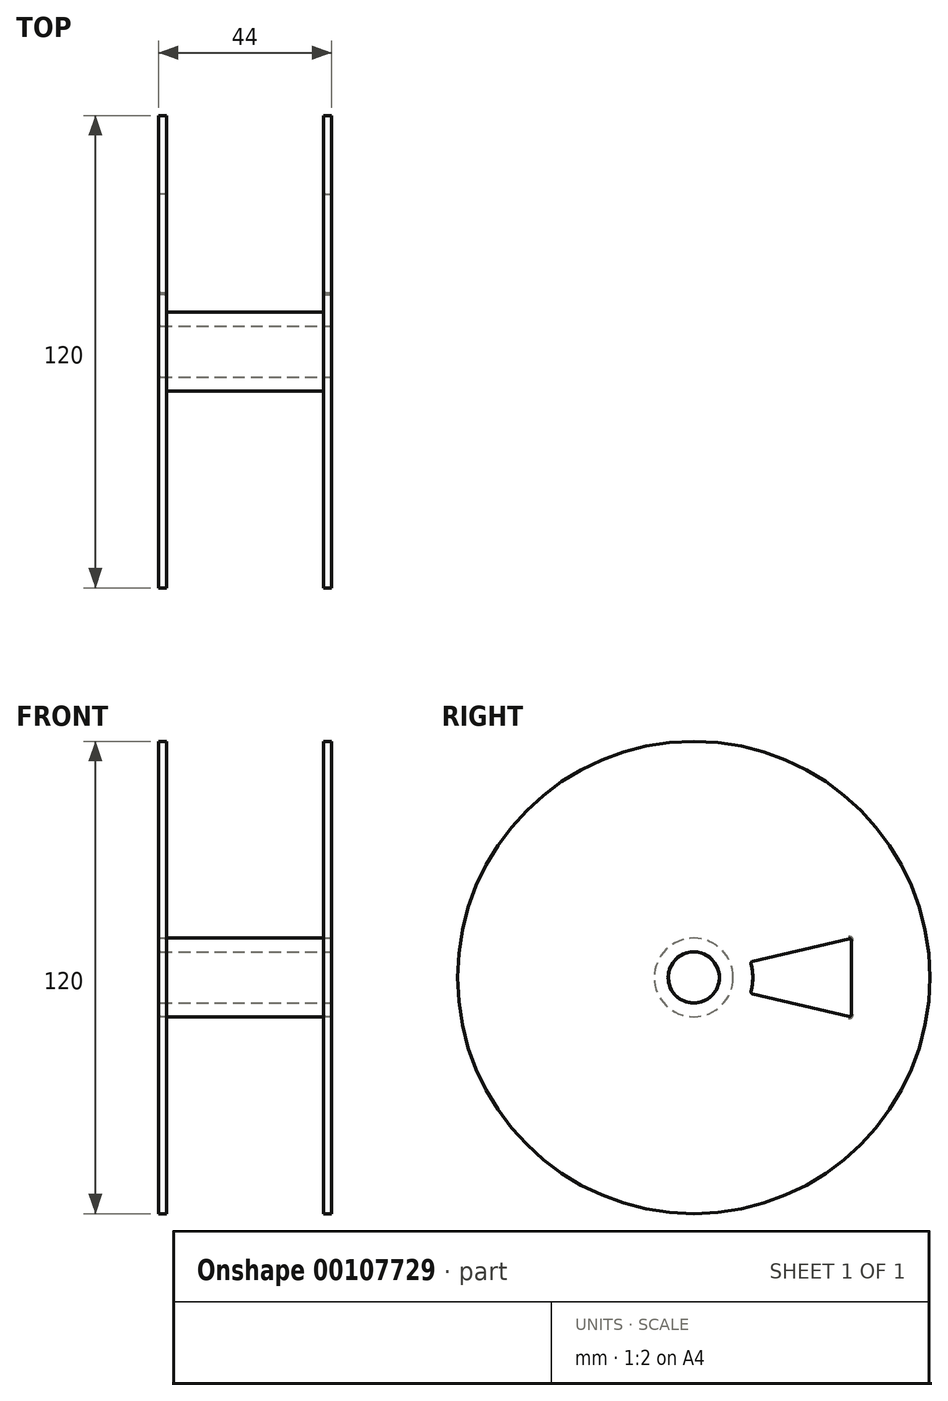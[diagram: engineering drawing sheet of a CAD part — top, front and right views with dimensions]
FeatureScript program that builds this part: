
annotation { "Feature Type Name" : "Feature", "Feature Type Description" : "" }
export const myFeature = defineFeature(function(context is Context, id is Id, definition is map)
    precondition{}
    {
        {
            var Q0;
            Q0=qCreatedBy(makeId("Front.planeOp"),FACE);
            var sketch = newSketch(context, id + "F0", { "sketchPlane" : qUnion([Q0])});
            skLineSegment(sketch, "E0", {"start": v(0, 0) * mm, "end": v(0, 10) * mm});
            skLineSegment(sketch, "E1", {"start": v(0, 10) * mm, "end": v(-20, 10) * mm});
            skLineSegment(sketch, "E2", {"start": v(-20, 10) * mm, "end": v(-20, 60) * mm});
            skLineSegment(sketch, "E3", {"start": v(-20, 60) * mm, "end": v(-22, 60) * mm});
            skLineSegment(sketch, "E4", {"start": v(-22, 60) * mm, "end": v(-22, 0) * mm});
            skLineSegment(sketch, "E5", {"start": v(-22, 0) * mm, "end": v(0, 0) * mm});
            skLineSegment(sketch, "E6.MirrorCS", {"start": v(20, 60) * mm, "end": v(22, 60) * mm});
            skLineSegment(sketch, "E7.MirrorCS", {"start": v(22, 0) * mm, "end": v(0, 0) * mm});
            skLineSegment(sketch, "E8.MirrorCS", {"start": v(20, 10) * mm, "end": v(20, 60) * mm});
            skLineSegment(sketch, "E9.MirrorCS", {"start": v(22, 60) * mm, "end": v(22, 0) * mm});
            skLineSegment(sketch, "E10.MirrorCS", {"start": v(0, 10) * mm, "end": v(20, 10) * mm});
            skSolve(sketch);
        }
        {
            var Q0;
            Q0 = qSketchRegion(id + "F0", true);
            var Q1;
            Q1=sQuery(id+"F0.wireOp",EDGE,"E5");
            revolve(context, id + "F1", {"entities" : qUnion([Q0]), "axis" : qUnion([Q1]), "revolveType" : RevolveType.FULL});
        }
        {
            var Q0;
            Q0=makeQuery(id+"F1.opRevolve","SWEPT_FACE",FACE,{"disambiguationData":[OSD([sQuery(id+"F0.wireOp",EDGE,"E9.MirrorCS")])]});
            var sketch = newSketch(context, id + "F2", { "sketchPlane" : qUnion([Q0])});
            skCircle(sketch, "E11", {"center": v(0, 0) * mm, "radius": 6.5 * mm});
            skSolve(sketch);
        }
        {
            var Q0;
            Q0 = qSketchRegion(id + "F2", true);
            extrude(context, id + "F3", {"entities" : qUnion([Q0]), "operationType" : NewBodyOperationType.REMOVE, "endBound" : BoundingType.THROUGH_ALL, "oppositeDirection" : true, "depth" : 25 * mm});
        }
        {
            var Q0;
            Q0=makeQuery(id+"F1.opRevolve","SWEPT_FACE",FACE,{"disambiguationData":[OSD([sQuery(id+"F0.wireOp",EDGE,"E9.MirrorCS")])]});
            var sketch = newSketch(context, id + "F4", { "sketchPlane" : qUnion([Q0])});
            skLineSegment(sketch, "E12", {"start": v(0, 0) * mm, "end": v(40, 0) * mm, "construction": true});
            skLineSegment(sketch, "E13", {"start": v(40, 10) * mm, "end": v(40, -10) * mm});
            skCircle(sketch, "E14.0", {"center": v(0, 0) * mm, "radius": 15 * mm});
            skLineSegment(sketch, "E15", {"start": v(40, 10) * mm, "end": v(14.46, 4) * mm});
            skLineSegment(sketch, "E16.MirrorCS", {"start": v(40, -10) * mm, "end": v(14.46, -4) * mm});
            skSolve(sketch);
        }
        {
            var Q0;
            Q0=makeQuery(id+"F4.imprint","IMPRINT",FACE,{"disambiguationData":[TD([[makeQuery(id+"F4.imprint","IMPRINT",EDGE,{"derivedFrom":sQuery(id+"F4.wireOp",EDGE,"E13")}),-1.0]])]});
            extrude(context, id + "F5", {"entities" : qUnion([Q0]), "operationType" : NewBodyOperationType.REMOVE, "endBound" : BoundingType.THROUGH_ALL, "oppositeDirection" : true, "depth" : 25 * mm});
        }
        {
            var Q0;
            Q0=makeQuery(id+"F5.boolean.opBoolean","COPY",EDGE,{"derivedFrom":makeQuery(id+"F5.opExtrude","CAP_EDGE",EDGE,{"disambiguationData":[OSD([sQuery(id+"F4.wireOp",EDGE,"E16.MirrorCS")])],"isStart":true})});
            var Q1;
            Q1=makeQuery(id+"F5.boolean.opBoolean","INTERSECT",EDGE,{"derivedFrom":[makeQuery(id+"F1.opRevolve","SWEPT_FACE",FACE,{"disambiguationData":[OSD([sQuery(id+"F0.wireOp",EDGE,"E8.MirrorCS")])]}),makeQuery(id+"F5.opExtrude","SWEPT_FACE",FACE,{"disambiguationData":[OSD([sQuery(id+"F4.wireOp",EDGE,"E13")])]})]});
            var Q2;
            Q2=makeQuery(id+"F5.boolean.opBoolean","COPY",EDGE,{"derivedFrom":makeQuery(id+"F5.opExtrude","CAP_EDGE",EDGE,{"disambiguationData":[OSD([sQuery(id+"F4.wireOp",EDGE,"E15")])],"isStart":true})});
            var Q3;
            Q3=makeQuery(id+"F5.boolean.opBoolean","INTERSECT",EDGE,{"derivedFrom":[makeQuery(id+"F1.opRevolve","SWEPT_FACE",FACE,{"disambiguationData":[OSD([sQuery(id+"F0.wireOp",EDGE,"E8.MirrorCS")])]}),makeQuery(id+"F5.opExtrude","SWEPT_FACE",FACE,{"disambiguationData":[OSD([sQuery(id+"F4.wireOp",EDGE,"E16.MirrorCS")])]})]});
            var Q4;
            Q4=makeQuery(id+"F5.boolean.opBoolean","INTERSECT",EDGE,{"derivedFrom":[makeQuery(id+"F1.opRevolve","SWEPT_FACE",FACE,{"disambiguationData":[OSD([sQuery(id+"F0.wireOp",EDGE,"E8.MirrorCS")])]}),makeQuery(id+"F5.opExtrude","SWEPT_FACE",FACE,{"disambiguationData":[OSD([sQuery(id+"F4.wireOp",EDGE,"E15")])]})]});
            var Q5;
            Q5=makeQuery(id+"F5.boolean.opBoolean","COPY",EDGE,{"derivedFrom":makeQuery(id+"F5.opExtrude","CAP_EDGE",EDGE,{"disambiguationData":[OSD([sQuery(id+"F4.wireOp",EDGE,"E14.0")])],"isStart":true})});
            var Q6;
            Q6=makeQuery(id+"F5.boolean.opBoolean","COPY",EDGE,{"derivedFrom":makeQuery(id+"F5.opExtrude","CAP_EDGE",EDGE,{"disambiguationData":[OSD([sQuery(id+"F4.wireOp",EDGE,"E13")])],"isStart":true})});
            var Q7;
            Q7=makeQuery(id+"F5.boolean.opBoolean","COPY",EDGE,{"disambiguationData":[OD(0.0)],"derivedFrom":makeQuery(id+"F5.opExtrude","SWEPT_EDGE",EDGE,{"disambiguationData":[OSD([sQuery(id+"F4.wireOp",EDGE,"E14.0"),sQuery(id+"F4.wireOp",EDGE,"E16.MirrorCS")])]})});
            var Q8;
            Q8=makeQuery(id+"F5.boolean.opBoolean","COPY",EDGE,{"disambiguationData":[OD(0.0)],"derivedFrom":makeQuery(id+"F5.opExtrude","SWEPT_EDGE",EDGE,{"disambiguationData":[OSD([sQuery(id+"F4.wireOp",EDGE,"E14.0"),sQuery(id+"F4.wireOp",EDGE,"E15")])]})});
            var Q9;
            Q9=makeQuery(id+"F5.boolean.opBoolean","COPY",EDGE,{"disambiguationData":[OD(0.0)],"derivedFrom":makeQuery(id+"F5.opExtrude","SWEPT_EDGE",EDGE,{"disambiguationData":[OSD([sQuery(id+"F4.wireOp",EDGE,"E13"),sQuery(id+"F4.wireOp",EDGE,"E15")])]})});
            var Q10;
            Q10=makeQuery(id+"F5.boolean.opBoolean","INTERSECT",EDGE,{"derivedFrom":[makeQuery(id+"F1.opRevolve","SWEPT_FACE",FACE,{"disambiguationData":[OSD([sQuery(id+"F0.wireOp",EDGE,"E2")])]}),makeQuery(id+"F5.opExtrude","SWEPT_FACE",FACE,{"disambiguationData":[OSD([sQuery(id+"F4.wireOp",EDGE,"E16.MirrorCS")])]})]});
            var Q11;
            Q11=makeQuery(id+"F5.boolean.opBoolean","INTERSECT",EDGE,{"derivedFrom":[makeQuery(id+"F1.opRevolve","SWEPT_FACE",FACE,{"disambiguationData":[OSD([sQuery(id+"F0.wireOp",EDGE,"E8.MirrorCS")])]}),makeQuery(id+"F5.opExtrude","SWEPT_FACE",FACE,{"disambiguationData":[OSD([sQuery(id+"F4.wireOp",EDGE,"E14.0")])]})]});
            var Q12;
            Q12=makeQuery(id+"F5.boolean.opBoolean","INTERSECT",EDGE,{"derivedFrom":[makeQuery(id+"F1.opRevolve","SWEPT_FACE",FACE,{"disambiguationData":[OSD([sQuery(id+"F0.wireOp",EDGE,"E4")])]}),makeQuery(id+"F5.opExtrude","SWEPT_FACE",FACE,{"disambiguationData":[OSD([sQuery(id+"F4.wireOp",EDGE,"E16.MirrorCS")])]})]});
            var Q13;
            Q13=makeQuery(id+"F5.boolean.opBoolean","COPY",EDGE,{"disambiguationData":[OD(0.0)],"derivedFrom":makeQuery(id+"F5.opExtrude","SWEPT_EDGE",EDGE,{"disambiguationData":[OSD([sQuery(id+"F4.wireOp",EDGE,"E13"),sQuery(id+"F4.wireOp",EDGE,"E16.MirrorCS")])]})});
            var Q14;
            Q14=makeQuery(id+"F5.boolean.opBoolean","COPY",EDGE,{"disambiguationData":[OD(1.0)],"derivedFrom":makeQuery(id+"F5.opExtrude","SWEPT_EDGE",EDGE,{"disambiguationData":[OSD([sQuery(id+"F4.wireOp",EDGE,"E14.0"),sQuery(id+"F4.wireOp",EDGE,"E16.MirrorCS")])]})});
            var Q15;
            Q15=makeQuery(id+"F5.boolean.opBoolean","COPY",EDGE,{"disambiguationData":[OD(1.0)],"derivedFrom":makeQuery(id+"F5.opExtrude","SWEPT_EDGE",EDGE,{"disambiguationData":[OSD([sQuery(id+"F4.wireOp",EDGE,"E13"),sQuery(id+"F4.wireOp",EDGE,"E16.MirrorCS")])]})});
            var Q16;
            Q16=makeQuery(id+"F5.boolean.opBoolean","INTERSECT",EDGE,{"derivedFrom":[makeQuery(id+"F1.opRevolve","SWEPT_FACE",FACE,{"disambiguationData":[OSD([sQuery(id+"F0.wireOp",EDGE,"E2")])]}),makeQuery(id+"F5.opExtrude","SWEPT_FACE",FACE,{"disambiguationData":[OSD([sQuery(id+"F4.wireOp",EDGE,"E15")])]})]});
            var Q17;
            Q17=makeQuery(id+"F5.boolean.opBoolean","INTERSECT",EDGE,{"derivedFrom":[makeQuery(id+"F1.opRevolve","SWEPT_FACE",FACE,{"disambiguationData":[OSD([sQuery(id+"F0.wireOp",EDGE,"E2")])]}),makeQuery(id+"F5.opExtrude","SWEPT_FACE",FACE,{"disambiguationData":[OSD([sQuery(id+"F4.wireOp",EDGE,"E14.0")])]})]});
            var Q18;
            Q18=makeQuery(id+"F5.boolean.opBoolean","INTERSECT",EDGE,{"derivedFrom":[makeQuery(id+"F1.opRevolve","SWEPT_FACE",FACE,{"disambiguationData":[OSD([sQuery(id+"F0.wireOp",EDGE,"E4")])]}),makeQuery(id+"F5.opExtrude","SWEPT_FACE",FACE,{"disambiguationData":[OSD([sQuery(id+"F4.wireOp",EDGE,"E15")])]})]});
            var Q19;
            Q19=makeQuery(id+"F5.boolean.opBoolean","INTERSECT",EDGE,{"derivedFrom":[makeQuery(id+"F1.opRevolve","SWEPT_FACE",FACE,{"disambiguationData":[OSD([sQuery(id+"F0.wireOp",EDGE,"E4")])]}),makeQuery(id+"F5.opExtrude","SWEPT_FACE",FACE,{"disambiguationData":[OSD([sQuery(id+"F4.wireOp",EDGE,"E14.0")])]})]});
            var Q20;
            Q20=makeQuery(id+"F5.boolean.opBoolean","INTERSECT",EDGE,{"derivedFrom":[makeQuery(id+"F1.opRevolve","SWEPT_FACE",FACE,{"disambiguationData":[OSD([sQuery(id+"F0.wireOp",EDGE,"E4")])]}),makeQuery(id+"F5.opExtrude","SWEPT_FACE",FACE,{"disambiguationData":[OSD([sQuery(id+"F4.wireOp",EDGE,"E13")])]})]});
            var Q21;
            Q21=makeQuery(id+"F5.boolean.opBoolean","INTERSECT",EDGE,{"derivedFrom":[makeQuery(id+"F1.opRevolve","SWEPT_FACE",FACE,{"disambiguationData":[OSD([sQuery(id+"F0.wireOp",EDGE,"E2")])]}),makeQuery(id+"F5.opExtrude","SWEPT_FACE",FACE,{"disambiguationData":[OSD([sQuery(id+"F4.wireOp",EDGE,"E13")])]})]});
            var Q22;
            Q22=makeQuery(id+"F5.boolean.opBoolean","COPY",EDGE,{"disambiguationData":[OD(1.0)],"derivedFrom":makeQuery(id+"F5.opExtrude","SWEPT_EDGE",EDGE,{"disambiguationData":[OSD([sQuery(id+"F4.wireOp",EDGE,"E14.0"),sQuery(id+"F4.wireOp",EDGE,"E15")])]})});
            var Q23;
            Q23=makeQuery(id+"F5.boolean.opBoolean","COPY",EDGE,{"disambiguationData":[OD(1.0)],"derivedFrom":makeQuery(id+"F5.opExtrude","SWEPT_EDGE",EDGE,{"disambiguationData":[OSD([sQuery(id+"F4.wireOp",EDGE,"E13"),sQuery(id+"F4.wireOp",EDGE,"E15")])]})});
            var Q24;
            Q24=makeQuery(id+"F3.boolean.opBoolean","COPY",EDGE,{"derivedFrom":makeQuery(id+"F3.opExtrude","CAP_EDGE",EDGE,{"disambiguationData":[OSD([sQuery(id+"F2.wireOp",EDGE,"E11")])],"isStart":true})});
            var Q25;
            Q25=makeQuery(id+"F3.boolean.opBoolean","INTERSECT",EDGE,{"derivedFrom":[makeQuery(id+"F1.opRevolve","SWEPT_FACE",FACE,{"disambiguationData":[OSD([sQuery(id+"F0.wireOp",EDGE,"E4")])]}),makeQuery(id+"F3.opExtrude","SWEPT_FACE",FACE,{"disambiguationData":[OSD([sQuery(id+"F2.wireOp",EDGE,"E11")])]})]});
            fillet(context, id + "F6", {"entities" : qUnion([Q0, Q1, Q2, Q3, Q4, Q5, Q6, Q7, Q8, Q9, Q10, Q11, Q12, Q13, Q14, Q15, Q16, Q17, Q18, Q19, Q20, Q21, Q22, Q23, Q24, Q25]), "radius" : 0.5 * mm, "tangentPropagation" : true, "rho" : 0.5, "crossSection" : FilletCrossSection.CONIC, "allowEdgeOverflow" : false});
        }
    });
